# Revit family: NLRS_57_AIR_UN_design-penthouse-combination-louvre-bdcn_LT_sacs
name_source: partatom
category: Air Terminals
units: mm (PartAtom-declared; Revit-internal decimal feet)

## family parameters
Always vertical = Yes
Cut with Voids When Loaded = No
Part Type = Normal
Room Calculation Point = No
Round Connector Dimension = Use Diameter
Shared = No
Work Plane-Based = No

## types (1)
- BDCNGO
    Assembly Code = 57.00
    Default Elevation = 200 mm  [stored 0.656168 ft]
    Description = Compacte combinatie design aluminium dakkap BDCN
    Manufacturer = Solid Air Climate Solutions
    Model = BDGNGO
    NLRS_C_content_datum_gewijzigd = 18-07-2025
    NLRS_C_content_provider = Solid Air Climate Solutions
    NLRS_C_content_versie = 1.22.01
    NLRS_C_description = Compacte combinatie design aluminium dakkap BDCN
    SACS_Data_Hidden = BDCN
    Type Comments = Width x L1 en Width x L2 = aansluitmaat!
    URL = https://solid-air.nl

note: [stored X ft] marks values corroborated as IEEE doubles in the binary element streams (Revit-internal decimal feet)

## geometry (parser evidence)
native form markers: Sweep x23
no freeform markers — native parametric forms only
